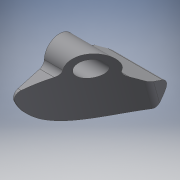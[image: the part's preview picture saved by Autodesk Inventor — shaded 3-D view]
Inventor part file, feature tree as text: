
AUTODESK INVENTOR PART (.ipt)
format: ipt  version: 2016 (Build 200138000, 138)  size: 166,912 bytes
history: native  units: in
note: dims shown in document units (in); Inventor stores cm internally (conversion verified against a paired STEP export)
features: extrude x2, sketch x2
ambient origin geometry x8: Origin, YZ Plane, XZ Plane, XY Plane, X Axis, Y Axis, Z Axis, Center Point
bodies: Solid1 (feature_tree)
feature tree (4):
  extrude  "Extrusion1"  Depth=0.0787in TaperAngle=0.0deg
  extrude  "Extrusion5"  Depth=0.0079in TaperAngle=0.0deg
  sketch  "Sketch1"  dims[d3=0.0236in d4=0.0787in d5=0.0in]
  sketch  "Sketch5"  dims[d10=0.0079in d18=0.1412in d19=0.0in]
